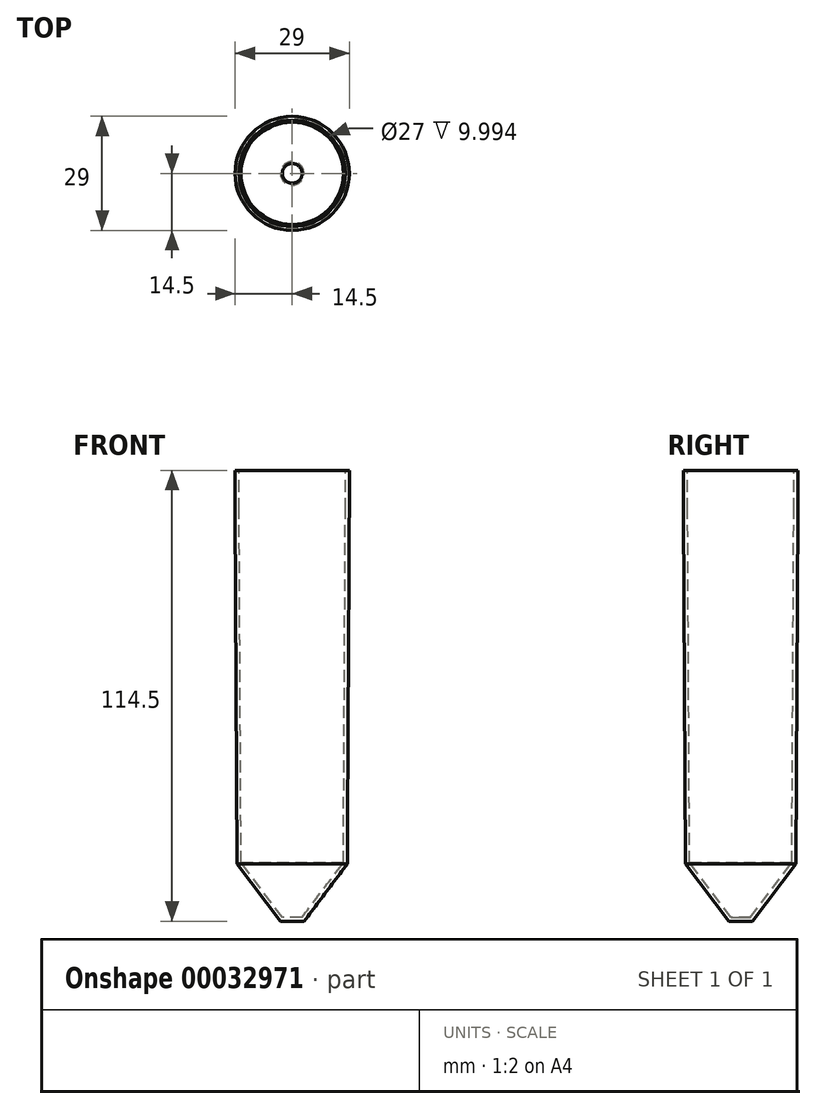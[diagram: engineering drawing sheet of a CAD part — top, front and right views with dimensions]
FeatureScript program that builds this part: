
annotation { "Feature Type Name" : "Feature", "Feature Type Description" : "" }
export const myFeature = defineFeature(function(context is Context, id is Id, definition is map)
    precondition{}
    {
        {
            var Q0;
            Q0=qCreatedBy(makeId("Front.planeOp"),FACE);
            var sketch = newSketch(context, id + "F0", { "sketchPlane" : qUnion([Q0])});
            skLineSegment(sketch, "E0.rect.bottom", {"start": v(14.5, -57.25) * mm, "end": v(-14.5, -57.25) * mm, "construction": true});
            skLineSegment(sketch, "E0.rect.top", {"start": v(14.5, 57.25) * mm, "end": v(-14.5, 57.25) * mm, "construction": true});
            skLineSegment(sketch, "E0.rect.left", {"start": v(14.5, -57.25) * mm, "end": v(14.5, 57.25) * mm, "construction": true});
            skLineSegment(sketch, "E0.rect.right", {"start": v(-14.5, -57.25) * mm, "end": v(-14.5, 57.25) * mm, "construction": true});
            skPoint(sketch, "E0.rect.middle", {"position": v(0, 0) * mm});
            skLineSegment(sketch, "E1", {"start": v(-14.5, 47.25) * mm, "end": v(14.5, 47.25) * mm, "construction": true});
            skLineSegment(sketch, "E2", {"start": v(-14.5, -42.75) * mm, "end": v(14.5, -42.75) * mm, "construction": true});
            skLineSegment(sketch, "E3", {"start": v(14, 65.57) * mm, "end": v(14, -66.16) * mm, "construction": true});
            skLineSegment(sketch, "E4", {"start": v(3, -35.53) * mm, "end": v(3, -60.32) * mm, "construction": true});
            skLineSegment(sketch, "E5", {"start": v(14, -42.75) * mm, "end": v(3, -57.25) * mm});
            skLineSegment(sketch, "E6", {"start": v(3, -57.25) * mm, "end": v(0, -57.25) * mm});
            skLineSegment(sketch, "E7", {"start": v(14.5, 57.25) * mm, "end": v(14.5, 47.25) * mm});
            skLineSegment(sketch, "E8", {"start": v(14.5, 47.25) * mm, "end": v(14, -42.75) * mm});
            skLineSegment(sketch, "E9.0", {"start": v(2.5, -56.25) * mm, "end": v(0, -56.25) * mm});
            skLineSegment(sketch, "E9.1", {"start": v(13, -42.41) * mm, "end": v(2.5, -56.25) * mm});
            skLineSegment(sketch, "E9.2", {"start": v(13.5, 47.26) * mm, "end": v(13, -42.41) * mm});
            skLineSegment(sketch, "E10", {"start": v(0, -57.25) * mm, "end": v(0, -56.25) * mm});
            skLineSegment(sketch, "E11", {"start": v(14.5, 57.25) * mm, "end": v(13.5, 57.25) * mm});
            skLineSegment(sketch, "E12", {"start": v(13.5, 57.25) * mm, "end": v(13.5, 47.26) * mm});
            skLineSegment(sketch, "E13", {"start": v(0, 80.91) * mm, "end": v(0, 0) * mm, "construction": true});
            skSolve(sketch);
        }
        {
            var Q0;
            Q0=qSketchRegion(id+"F0",true);
            var Q1;
            Q1=sQuery(id+"F0.wireOp",EDGE,"E13");
            revolve(context, id + "F1", {"entities" : qUnion([Q0]), "axis" : qUnion([Q1]), "revolveType" : RevolveType.FULL});
        }
    });
